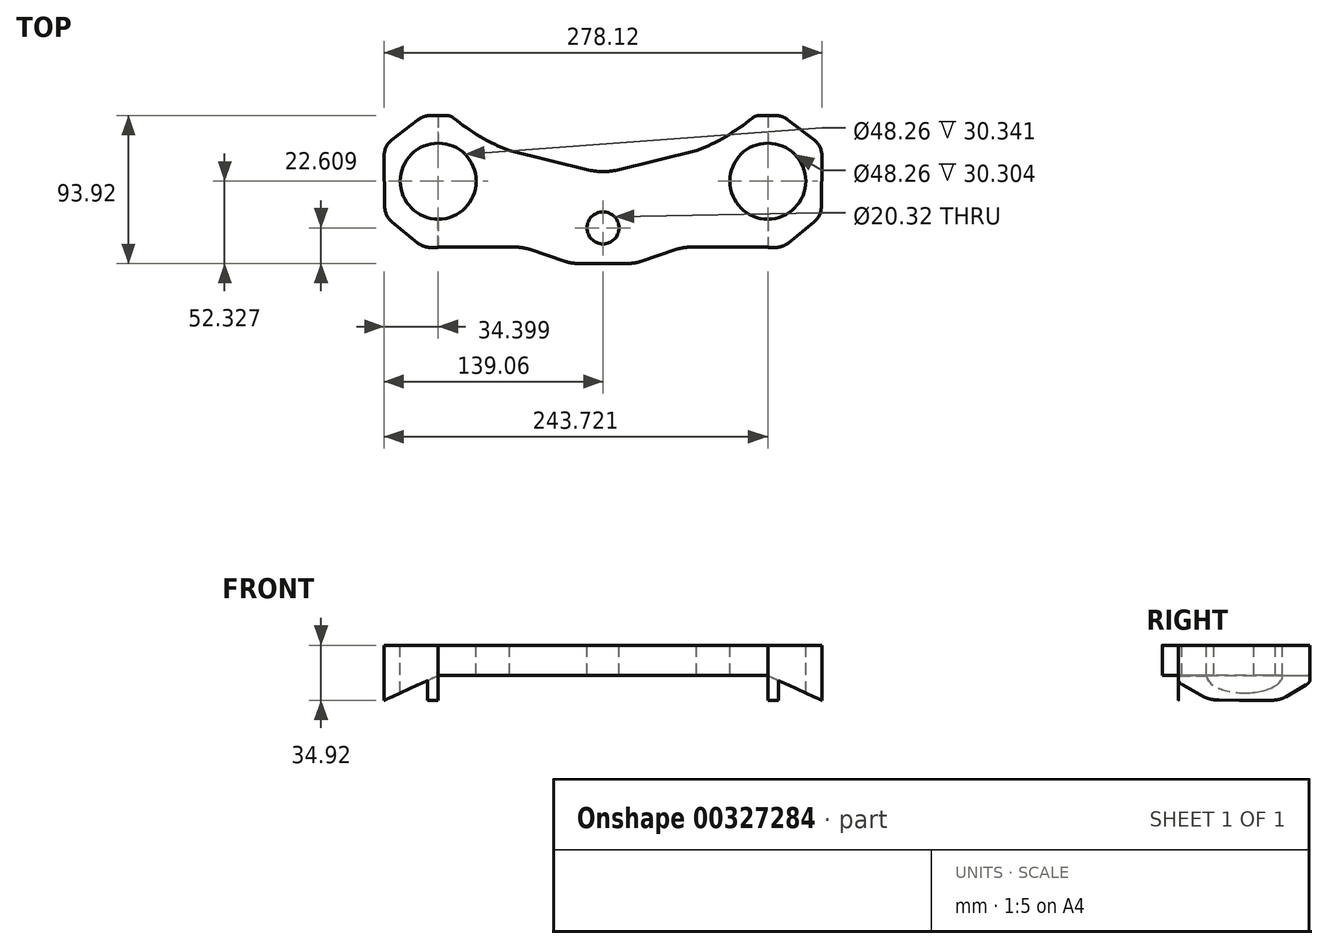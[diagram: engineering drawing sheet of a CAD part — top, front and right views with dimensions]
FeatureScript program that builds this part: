
annotation { "Feature Type Name" : "Feature", "Feature Type Description" : "" }
export const myFeature = defineFeature(function(context is Context, id is Id, definition is map)
    precondition{}
    {
        {
            var Q0;
            Q0=qCreatedBy(makeId("Top.planeOp"),FACE);
            var sketch = newSketch(context, id + "F0", { "sketchPlane" : qUnion([Q0])});
            skPoint(sketch, "E0.middle", {"position": v(0, 0) * mm});
            skArc(sketch, "E1", {"start": v(-104.66, -13.68) * mm, "mid": v(-80.53, 10.45) * mm, "end": v(-104.66, 34.58) * mm});
            skArc(sketch, "E2.MirrorC", {"start": v(104.66, -13.68) * mm, "mid": v(80.53, 10.45) * mm, "end": v(104.66, 34.58) * mm});
            skPoint(sketch, "E3.orphan", {"position": v(-24.04, -41.88) * mm});
            skPoint(sketch, "E4.MirrorCS.end.orphan", {"position": v(-19.99, -40.6) * mm});
            skLineSegment(sketch, "E5", {"start": v(-104.66, -20.43) * mm, "end": v(-104.66, -31.54) * mm});
            skLineSegment(sketch, "E6", {"start": v(-104.66, 40.93) * mm, "end": v(-104.66, 52.04) * mm});
            skLineSegment(sketch, "E7", {"start": v(-104.66, 52.04) * mm, "end": v(-98.91, 52.04) * mm});
            skLineSegment(sketch, "E8", {"start": v(-106.07, 40.93) * mm, "end": v(-106.08, 40.9) * mm});
            skLineSegment(sketch, "E9.MirrorCS", {"start": v(104.66, 40.93) * mm, "end": v(104.66, 52.04) * mm});
            skLineSegment(sketch, "E10.MirrorCS", {"start": v(104.66, -20.43) * mm, "end": v(104.66, -31.54) * mm});
            skLineSegment(sketch, "E11", {"start": v(-104.66, 40.93) * mm, "end": v(-104.66, 34.58) * mm});
            skLineSegment(sketch, "E12.trimOffspring", {"start": v(-104.66, -13.68) * mm, "end": v(-104.66, -20.43) * mm});
            skLineSegment(sketch, "E13", {"start": v(104.66, 40.93) * mm, "end": v(104.66, 34.58) * mm});
            skLineSegment(sketch, "E14.trimOffspring", {"start": v(104.66, -13.68) * mm, "end": v(104.66, -20.43) * mm});
            skPoint(sketch, "E15.MirrorCS.end.orphan", {"position": v(38.03, -31.54) * mm});
            skPoint(sketch, "E15.MirrorCS.start.orphan", {"position": v(104.66, -31.54) * mm});
            skPoint(sketch, "E16.trimOffspring.start.orphan", {"position": v(33.98, -31.87) * mm});
            skPoint(sketch, "E17.filletArc.start.orphan", {"position": v(19.99, -40.6) * mm});
            skPoint(sketch, "E18.start.orphan", {"position": v(24.04, -41.88) * mm});
            skPoint(sketch, "E19.filletArc.start.orphan", {"position": v(-33.98, -31.87) * mm});
            skPoint(sketch, "E20.end.orphan", {"position": v(-38.03, -31.54) * mm});
            skPoint(sketch, "E21.orphan", {"position": v(0, -41.88) * mm});
            skPoint(sketch, "E22.MirrorCS.start.orphan", {"position": v(50.43, -31.54) * mm});
            skPoint(sketch, "E23.end.orphan", {"position": v(-50.43, -31.54) * mm});
            skLineSegment(sketch, "E24", {"start": v(-15.87, -41.88) * mm, "end": v(15.87, -41.88) * mm});
            skLineSegment(sketch, "E25", {"start": v(-47.12, -32.84) * mm, "end": v(-23.9, -40.58) * mm});
            skLineSegment(sketch, "E26", {"start": v(-104.66, -31.54) * mm, "end": v(-55.14, -31.54) * mm});
            skLineSegment(sketch, "E27.MirrorCS", {"start": v(104.66, -31.54) * mm, "end": v(55.14, -31.54) * mm});
            skLineSegment(sketch, "E28.MirrorCS", {"start": v(47.12, -32.84) * mm, "end": v(23.9, -40.58) * mm});
            skPoint(sketch, "E29.visualSharp", {"position": v(-51.02, -31.54) * mm});
            skArc(sketch, "E29.filletArc", {"start": v(-47.12, -32.84) * mm, "mid": v(-51.08, -31.87) * mm, "end": v(-55.14, -31.54) * mm});
            skPoint(sketch, "E30.visualSharp", {"position": v(51.02, -31.54) * mm});
            skArc(sketch, "E30.filletArc", {"start": v(55.14, -31.54) * mm, "mid": v(51.08, -31.87) * mm, "end": v(47.12, -32.84) * mm});
            skPoint(sketch, "E31.visualSharp", {"position": v(19.99, -41.88) * mm});
            skArc(sketch, "E31.filletArc", {"start": v(15.87, -41.88) * mm, "mid": v(19.93, -41.55) * mm, "end": v(23.9, -40.58) * mm});
            skPoint(sketch, "E32.visualSharp", {"position": v(-19.99, -41.88) * mm});
            skArc(sketch, "E32.filletArc", {"start": v(-23.9, -40.58) * mm, "mid": v(-19.93, -41.55) * mm, "end": v(-15.87, -41.88) * mm});
            skPoint(sketch, "E33.filletArc.start.orphan", {"position": v(-88.65, 49.25) * mm});
            skPoint(sketch, "E34.start.orphan", {"position": v(-61.45, 34.33) * mm});
            skPoint(sketch, "E35.MirrorCS.end.orphan", {"position": v(61.45, 34.33) * mm});
            skPoint(sketch, "E35.MirrorCS.start.orphan", {"position": v(88.65, 49.25) * mm});
            skPoint(sketch, "E36.MirrorCS.end.orphan", {"position": v(96.6, 52.04) * mm});
            skLineSegment(sketch, "E37", {"start": v(-59.47, 29.85) * mm, "end": v(-9.07, 17.5) * mm});
            skArc(sketch, "E38", {"start": v(-94.86, 50.58) * mm, "mid": v(-78, 38.78) * mm, "end": v(-59.47, 29.85) * mm});
            skPoint(sketch, "E39.visualSharp", {"position": v(-96.6, 52.04) * mm});
            skArc(sketch, "E39.filletArc", {"start": v(-94.86, 50.58) * mm, "mid": v(-96.76, 51.66) * mm, "end": v(-98.91, 52.04) * mm});
            skLineSegment(sketch, "E40.MirrorCS", {"start": v(59.47, 29.85) * mm, "end": v(9.07, 17.5) * mm});
            skArc(sketch, "E41.MirrorCS", {"start": v(94.86, 50.58) * mm, "mid": v(78, 38.78) * mm, "end": v(59.47, 29.85) * mm});
            skArc(sketch, "E42.MirrorCS", {"start": v(94.86, 50.58) * mm, "mid": v(96.76, 51.66) * mm, "end": v(98.91, 52.04) * mm});
            skLineSegment(sketch, "E43.MirrorCS", {"start": v(104.66, 52.04) * mm, "end": v(98.91, 52.04) * mm});
            skPoint(sketch, "E44.visualSharp", {"position": v(0, 15.27) * mm});
            skArc(sketch, "E44.filletArc", {"start": v(-9.07, 17.5) * mm, "mid": v(0, 16.4) * mm, "end": v(9.07, 17.5) * mm});
            skCircle(sketch, "E45", {"center": v(0, -19.27) * mm, "radius": 10.16 * mm});
            skSolve(sketch);
        }
        {
            var Q0;
            Q0=qCreatedBy(makeId("Top.planeOp"),FACE);
            var sketch = newSketch(context, id + "F1", { "sketchPlane" : qUnion([Q0])});
            skArc(sketch, "E46", {"start": v(-104.66, 34.58) * mm, "mid": v(-128.8, 10.45) * mm, "end": v(-104.66, -13.68) * mm});
            skLineSegment(sketch, "E47", {"start": v(-104.66, 52.04) * mm, "end": v(-104.66, 34.58) * mm});
            skPoint(sketch, "E48.MirrorCS.end.orphan", {"position": v(-104.66, -29.09) * mm});
            skPoint(sketch, "E48.MirrorCS.start.orphan", {"position": v(-114.19, -52.04) * mm});
            skPoint(sketch, "E49.visualSharp", {"position": v(-114.19, 52.04) * mm});
            skPoint(sketch, "E50.visualSharp", {"position": v(-114.19, -31.65) * mm});
            skPoint(sketch, "E51.visualSharp", {"position": v(-104.66, 0.9) * mm});
            skPoint(sketch, "E52.visualSharp", {"position": v(-104.66, 29.09) * mm});
            skPoint(sketch, "E53.start.orphan", {"position": v(-104.66, -31.65) * mm});
            skLineSegment(sketch, "E54", {"start": v(-109.83, 52.04) * mm, "end": v(-104.66, 52.04) * mm});
            skLineSegment(sketch, "E55", {"start": v(-109.66, -31.65) * mm, "end": v(-104.66, -31.65) * mm});
            skLineSegment(sketch, "E56", {"start": v(-139.05, 26.35) * mm, "end": v(-138.63, -5.85) * mm});
            skLineSegment(sketch, "E57", {"start": v(-117.62, 49.37) * mm, "end": v(-134.14, 36.55) * mm});
            skLineSegment(sketch, "E58", {"start": v(-133.96, -15.52) * mm, "end": v(-117.7, -28.8) * mm});
            skArc(sketch, "E59.filletArc", {"start": v(-109.83, 52.04) * mm, "mid": v(-113.95, 51.35) * mm, "end": v(-117.62, 49.37) * mm});
            skArc(sketch, "E60.filletArc", {"start": v(-117.7, -28.8) * mm, "mid": v(-113.92, -30.92) * mm, "end": v(-109.66, -31.65) * mm});
            skPoint(sketch, "E61.visualSharp", {"position": v(-138.56, -11.78) * mm});
            skArc(sketch, "E61.filletArc", {"start": v(-138.63, -5.85) * mm, "mid": v(-137.37, -11.2) * mm, "end": v(-133.96, -15.52) * mm});
            skPoint(sketch, "E62.visualSharp", {"position": v(-139.14, 32.67) * mm});
            skArc(sketch, "E62.filletArc", {"start": v(-134.14, 36.55) * mm, "mid": v(-137.8, 32.03) * mm, "end": v(-139.05, 26.35) * mm});
            skPoint(sketch, "E63.0.center.orphan", {"position": v(-104.66, 10.92) * mm});
            skPoint(sketch, "E64.start.orphan", {"position": v(-104.66, 33.15) * mm});
            skPoint(sketch, "E65.trimOffspring.end.orphan", {"position": v(-104.66, -11.3) * mm});
            skLineSegment(sketch, "E66.trimOffspring", {"start": v(-104.66, -31.65) * mm, "end": v(-104.66, -53.56) * mm});
            skLineSegment(sketch, "E67", {"start": v(-104.66, -31.65) * mm, "end": v(-104.66, -13.68) * mm});
            skLineSegment(sketch, "E68.MirrorCS", {"start": v(109.83, 52.04) * mm, "end": v(104.66, 52.04) * mm});
            skArc(sketch, "E69.MirrorCS", {"start": v(109.83, 52.04) * mm, "mid": v(113.95, 51.35) * mm, "end": v(117.62, 49.37) * mm});
            skLineSegment(sketch, "E70.MirrorCS", {"start": v(117.62, 49.37) * mm, "end": v(134.14, 36.55) * mm});
            skArc(sketch, "E71.MirrorCS", {"start": v(134.14, 36.55) * mm, "mid": v(137.8, 32.03) * mm, "end": v(139.05, 26.35) * mm});
            skLineSegment(sketch, "E72.MirrorCS", {"start": v(139.05, 26.35) * mm, "end": v(138.63, -5.85) * mm});
            skLineSegment(sketch, "E73.MirrorCS", {"start": v(104.66, 52.04) * mm, "end": v(104.66, 34.58) * mm});
            skArc(sketch, "E74.MirrorCS", {"start": v(104.66, 34.58) * mm, "mid": v(128.8, 10.45) * mm, "end": v(104.66, -13.68) * mm});
            skLineSegment(sketch, "E75.MirrorCS", {"start": v(104.66, -31.65) * mm, "end": v(104.66, -13.68) * mm});
            skLineSegment(sketch, "E76.MirrorCS", {"start": v(109.66, -31.65) * mm, "end": v(104.66, -31.65) * mm});
            skArc(sketch, "E77.MirrorCS", {"start": v(117.7, -28.8) * mm, "mid": v(113.92, -30.92) * mm, "end": v(109.66, -31.65) * mm});
            skLineSegment(sketch, "E78.MirrorCS", {"start": v(133.96, -15.52) * mm, "end": v(117.7, -28.8) * mm});
            skArc(sketch, "E79.MirrorCS", {"start": v(138.63, -5.85) * mm, "mid": v(137.37, -11.2) * mm, "end": v(133.96, -15.52) * mm});
            skSolve(sketch);
        }
        {
            var Q0;
            Q0=makeQuery(id+"F0.imprint","IMPRINT",FACE,{"disambiguationData":[TD([[makeQuery(id+"F0.imprint","IMPRINT",EDGE,{"derivedFrom":sQuery(id+"F0.wireOp",EDGE,"E1")}),-1.0]])]});
            extrude(context, id + "F2", {"entities" : qUnion([Q0]), "oppositeDirection" : true, "depth" : 19.05 * mm});
        }
        {
            var Q0;
            Q0=makeQuery(id+"F1.imprint","IMPRINT",FACE,{"disambiguationData":[TD([[makeQuery(id+"F1.imprint","IMPRINT",EDGE,{"derivedFrom":sQuery(id+"F1.wireOp",EDGE,"E46")}),-1.0]])]});
            var Q1;
            Q1=makeQuery(id+"F1.imprint","IMPRINT",FACE,{"disambiguationData":[TD([[makeQuery(id+"F1.imprint","IMPRINT",EDGE,{"derivedFrom":sQuery(id+"F1.wireOp",EDGE,"E68.MirrorCS")}),1.0]])]});
            extrude(context, id + "F3", {"entities" : qUnion([Q0, Q1]), "operationType" : NewBodyOperationType.ADD, "oppositeDirection" : true, "depth" : 34.92 * mm});
        }
        {
            var Q0;
            Q0=qCreatedBy(makeId("Front.planeOp"),FACE);
            cPlane(context, id + "F4", {"entities" : qUnion([Q0]), "cplaneType" : CPlaneType.OFFSET, "offset" : 31.55 * mm, "width" : 152.4 * mm, "height" : 152.4 * mm});
        }
        {
            var Q0;
            Q0=qCreatedBy(id+"F4.planeOp",FACE);
            var sketch = newSketch(context, id + "F5", { "sketchPlane" : qUnion([Q0])});
            skLineSegment(sketch, "E80.left", {"start": v(-104.72, -19.36) * mm, "end": v(-104.72, -34.86) * mm});
            skLineSegment(sketch, "E81", {"start": v(-138.8, -34.86) * mm, "end": v(-104.72, -19.36) * mm});
            skLineSegment(sketch, "E82.bottom", {"start": v(-104.72, -19.36) * mm, "end": v(-97.3, -19.36) * mm});
            skLineSegment(sketch, "E82.top", {"start": v(-104.72, -38.74) * mm, "end": v(-97.3, -38.74) * mm});
            skLineSegment(sketch, "E82.right", {"start": v(-97.3, -19.36) * mm, "end": v(-97.3, -38.74) * mm});
            skLineSegment(sketch, "E83.top", {"start": v(-138.8, -39.62) * mm, "end": v(-104.72, -39.62) * mm});
            skLineSegment(sketch, "E83.left", {"start": v(-138.8, -34.86) * mm, "end": v(-138.8, -39.62) * mm});
            skLineSegment(sketch, "E83.right", {"start": v(-104.72, -38.74) * mm, "end": v(-104.72, -39.62) * mm});
            skPoint(sketch, "E84.MirrorCS.end.orphan", {"position": v(104.72, -19.36) * mm});
            skPoint(sketch, "E84.MirrorCS.start.orphan", {"position": v(138.8, -34.86) * mm});
            skPoint(sketch, "E85.MirrorCS.end.orphan", {"position": v(104.72, -34.86) * mm});
            skLineSegment(sketch, "E86.MirrorCS", {"start": v(97.3, -19.36) * mm, "end": v(97.3, -38.74) * mm});
            skLineSegment(sketch, "E87.MirrorCS", {"start": v(104.72, -19.36) * mm, "end": v(97.3, -19.36) * mm});
            skLineSegment(sketch, "E88.MirrorCS", {"start": v(138.8, -34.86) * mm, "end": v(104.72, -19.36) * mm});
            skLineSegment(sketch, "E89.MirrorCS", {"start": v(138.8, -34.86) * mm, "end": v(138.8, -39.62) * mm});
            skLineSegment(sketch, "E90.MirrorCS", {"start": v(138.8, -39.62) * mm, "end": v(104.72, -39.62) * mm});
            skLineSegment(sketch, "E91.MirrorCS", {"start": v(104.72, -38.74) * mm, "end": v(97.3, -38.74) * mm});
            skLineSegment(sketch, "E92.MirrorCS", {"start": v(104.72, -38.74) * mm, "end": v(104.72, -39.62) * mm});
            skSolve(sketch);
        }
        {
            var Q0;
            Q0 = qSketchRegion(id + "F5", true);
            extrude(context, id + "F6", {"entities" : qUnion([Q0]), "operationType" : NewBodyOperationType.REMOVE, "oppositeDirection" : true, "depth" : 101.6 * mm});
        }
        {
            var Q0;
            Q0 = qSketchRegion(id + "F5", true);
            extrude(context, id + "F7", {"entities" : qUnion([Q0]), "operationType" : NewBodyOperationType.REMOVE, "oppositeDirection" : true, "depth" : 101.6 * mm});
        }
    });
